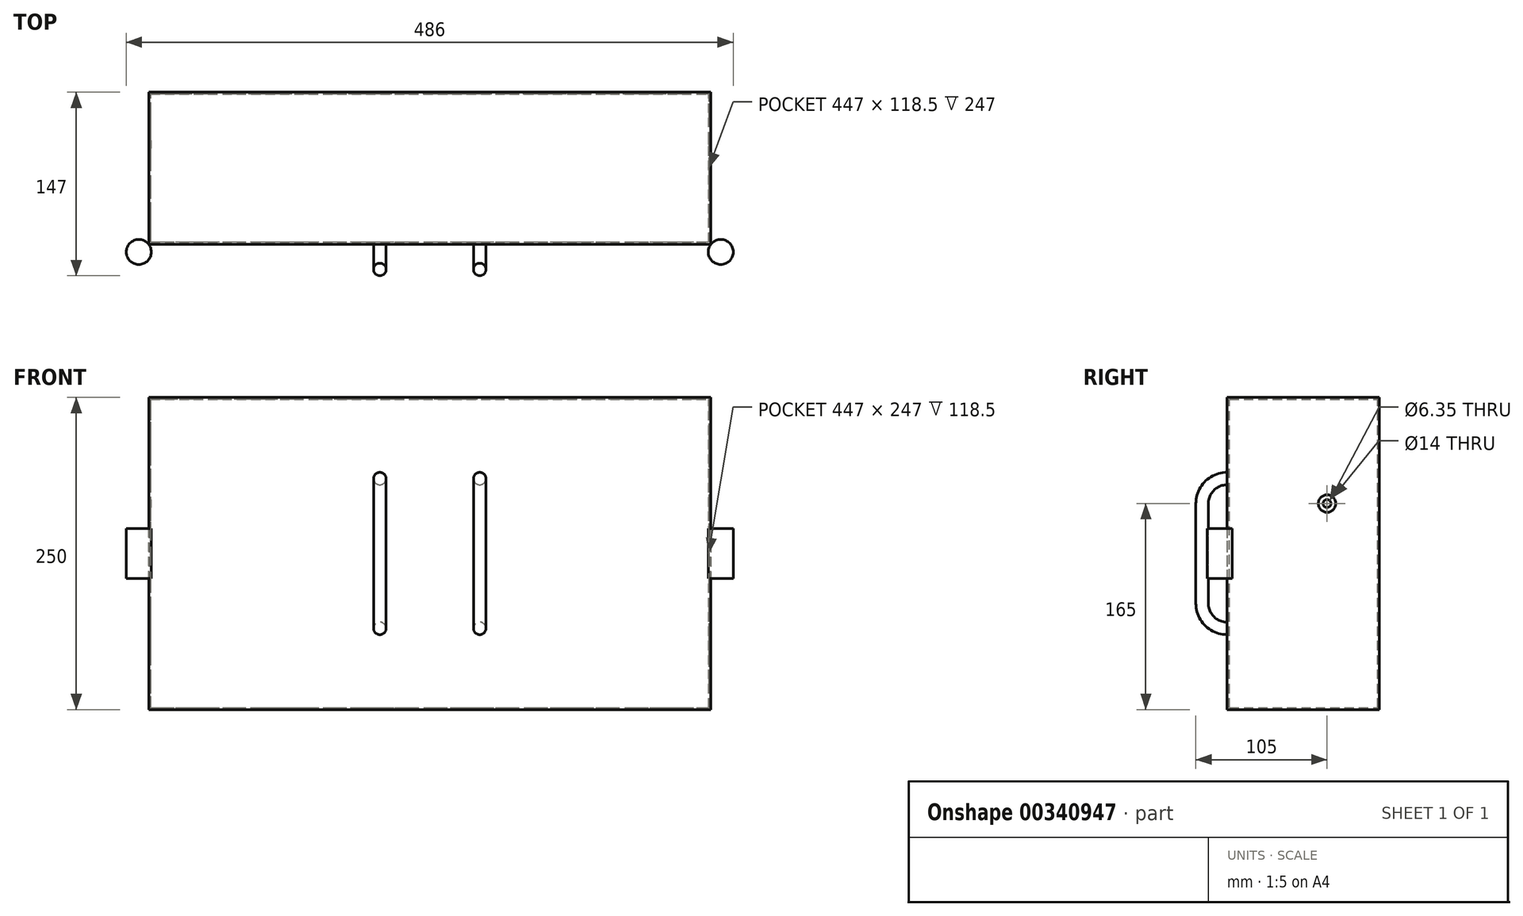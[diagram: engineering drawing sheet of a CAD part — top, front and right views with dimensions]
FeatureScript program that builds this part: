
annotation { "Feature Type Name" : "Feature", "Feature Type Description" : "" }
export const myFeature = defineFeature(function(context is Context, id is Id, definition is map)
    precondition{}
    {
        {
            var Q0;
            Q0=qCreatedBy(makeId("Front.planeOp"),FACE);
            var sketch = newSketch(context, id + "F0", { "sketchPlane" : qUnion([Q0])});
            skLineSegment(sketch, "E0.bottom", {"start": v(-225, -125) * mm, "end": v(225, -125) * mm});
            skLineSegment(sketch, "E0.top", {"start": v(-225, 125) * mm, "end": v(225, 125) * mm});
            skLineSegment(sketch, "E0.left", {"start": v(-225, -125) * mm, "end": v(-225, 125) * mm});
            skLineSegment(sketch, "E0.right", {"start": v(225, -125) * mm, "end": v(225, 125) * mm});
            skPoint(sketch, "E0.middle", {"position": v(0, 0) * mm});
            skSolve(sketch);
        }
        {
            var Q0;
            Q0 = qSketchRegion(id + "F0", true);
            extrude(context, id + "F1", {"entities" : qUnion([Q0]), "depth" : 120 * mm});
        }
        {
            var Q0;
            Q0=makeQuery(id+"F1.opExtrude","CAP_FACE",FACE,{"disambiguationData":[OSD([sQuery(id+"F0.wireOp",EDGE,"E0.bottom"),sQuery(id+"F0.wireOp",EDGE,"E0.top"),sQuery(id+"F0.wireOp",EDGE,"E0.left"),sQuery(id+"F0.wireOp",EDGE,"E0.right")])],"isStart":false});
            shell(context, id + "F2", {"entities" : qUnion([Q0]), "thickness" : 1.5 * mm});
        }
        {
            var Q0;
            Q0=makeQuery(id+"F1.opExtrude","SWEPT_FACE",FACE,{"disambiguationData":[OSD([sQuery(id+"F0.wireOp",EDGE,"E0.left")])]});
            var sketch = newSketch(context, id + "F3", { "sketchPlane" : qUnion([Q0])});
            skCircle(sketch, "E1", {"center": v(42, 40) * mm, "radius": 3.18 * mm});
            skSolve(sketch);
        }
        {
            var Q0;
            Q0 = qSketchRegion(id + "F3", true);
            extrude(context, id + "F4", {"entities" : qUnion([Q0]), "operationType" : NewBodyOperationType.REMOVE, "oppositeDirection" : true, "depth" : 555 * mm});
        }
        {
            var Q0;
            Q0=makeQuery(id+"F1.opExtrude","SWEPT_FACE",FACE,{"disambiguationData":[OSD([sQuery(id+"F0.wireOp",EDGE,"E0.right")])]});
            var sketch = newSketch(context, id + "F5", { "sketchPlane" : qUnion([Q0])});
            skCircle(sketch, "E2", {"center": v(-42, 40) * mm, "radius": 7 * mm});
            skSolve(sketch);
        }
        {
            var Q0;
            Q0 = qSketchRegion(id + "F5", true);
            extrude(context, id + "F6", {"entities" : qUnion([Q0]), "operationType" : NewBodyOperationType.REMOVE, "oppositeDirection" : true, "depth" : 5 * mm});
        }
        {
            var Q0;
            Q0=qCreatedBy(makeId("Top.planeOp"),FACE);
            var sketch = newSketch(context, id + "F7", { "sketchPlane" : qUnion([Q0])});
            skCircle(sketch, "E3", {"center": v(-233, -128) * mm, "radius": 10 * mm});
            skLineSegment(sketch, "E4.0", {"start": v(-225, -120) * mm, "end": v(-225, 0) * mm});
            skLineSegment(sketch, "E5.0", {"start": v(-225, -120) * mm, "end": v(225, -120) * mm});
            skCircle(sketch, "E6", {"center": v(233, -128) * mm, "radius": 10 * mm});
            skLineSegment(sketch, "E7", {"start": v(-225, -120) * mm, "end": v(-225, -122) * mm});
            skLineSegment(sketch, "E8", {"start": v(225, -120) * mm, "end": v(225, -122) * mm});
            skLineSegment(sketch, "E9", {"start": v(225, -122) * mm, "end": v(-225, -122) * mm});
            skSolve(sketch);
        }
        {
            var Q0;
            Q0=makeQuery(id+"F7.imprint","IMPRINT",FACE,{"disambiguationData":[TD([[makeQuery(id+"F7.imprint","IMPRINT",EDGE,{"derivedFrom":sQuery(id+"F7.wireOp",EDGE,"E5.0")}),-1.0]])]});
            var Q1;
            Q1=makeQuery(id+"F1.opExtrude","SWEPT_FACE",FACE,{"disambiguationData":[OSD([sQuery(id+"F0.wireOp",EDGE,"E0.top")])]});
            var Q2;
            Q2=makeQuery(id+"F1.opExtrude","SWEPT_FACE",FACE,{"disambiguationData":[OSD([sQuery(id+"F0.wireOp",EDGE,"E0.bottom")])]});
            extrude(context, id + "F8", {"entities" : qUnion([Q0]), "operationType" : NewBodyOperationType.ADD, "endBound" : BoundingType.UP_TO_SURFACE, "endBoundEntityFace" : qUnion([Q1]), "depth" : 25 * mm, "hasSecondDirection" : true, "secondDirectionBound" : SecondDirectionBoundingType.UP_TO_SURFACE, "secondDirectionOppositeDirection" : true, "secondDirectionBoundEntityFace" : qUnion([Q2]), "secondDirectionDepth" : 25 * mm});
        }
        {
            var Q0;
            Q0=qCreatedBy(makeId("Right.planeOp"),FACE);
            cPlane(context, id + "F9", {"entities" : qUnion([Q0]), "cplaneType" : CPlaneType.OFFSET, "offset" : 40 * mm, "width" : 150 * mm, "height" : 150 * mm});
        }
        {
            var Q0;
            Q0=qCreatedBy(id+"F9.planeOp",FACE);
            var sketch = newSketch(context, id + "F10", { "sketchPlane" : qUnion([Q0])});
            skArc(sketch, "E10.0", {"start": v(-121.76, 60) * mm, "mid": v(-136.06, 54.23) * mm, "end": v(-142, 40) * mm});
            skLineSegment(sketch, "E11.0", {"start": v(-142, 40) * mm, "end": v(-142, -40) * mm});
            skArc(sketch, "E12.0", {"start": v(-142, -40) * mm, "mid": v(-136.06, -54.23) * mm, "end": v(-121.76, -60) * mm});
            skSolve(sketch);
        }
        {
            var Q0;
            Q0=qCreatedBy(makeId("Right.planeOp"),FACE);
            cPlane(context, id + "F11", {"entities" : qUnion([Q0]), "cplaneType" : CPlaneType.OFFSET, "offset" : 40 * mm, "oppositeDirection" : true, "width" : 150 * mm, "height" : 150 * mm});
        }
        {
            var Q0;
            Q0=qCreatedBy(id+"F11.planeOp",FACE);
            var sketch = newSketch(context, id + "F12", { "sketchPlane" : qUnion([Q0])});
            skArc(sketch, "E13.0", {"start": v(-121.76, 60) * mm, "mid": v(-136.06, 54.23) * mm, "end": v(-142, 40) * mm});
            skLineSegment(sketch, "E14.0", {"start": v(-142, 40) * mm, "end": v(-142, -40) * mm});
            skPoint(sketch, "E15.0", {"position": v(-136.06, -54.23) * mm});
            skArc(sketch, "E16.0", {"start": v(-142, -40) * mm, "mid": v(-136.06, -54.23) * mm, "end": v(-121.76, -60) * mm});
            skSolve(sketch);
        }
        {
            var Q0;
            Q0=makeQuery(id+"F8.opExtrude","SWEPT_FACE",FACE,{"disambiguationData":[OSD([sQuery(id+"F7.wireOp",EDGE,"E9")])]});
            var sketch = newSketch(context, id + "F13", { "sketchPlane" : qUnion([Q0])});
            skPoint(sketch, "E17.0", {"position": v(-40, -60) * mm});
            skPoint(sketch, "E18.0", {"position": v(40, -60) * mm});
            skCircle(sketch, "E19", {"center": v(-40, -60) * mm, "radius": 5 * mm});
            skCircle(sketch, "E20", {"center": v(40, -60) * mm, "radius": 5 * mm});
            skSolve(sketch);
        }
        {
            var Q0;
            Q0=makeQuery(id+"F13.imprint","IMPRINT",FACE,{"disambiguationData":[TD([[makeQuery(id+"F13.imprint","IMPRINT",EDGE,{"derivedFrom":sQuery(id+"F13.wireOp",EDGE,"E19")}),1.0]])]});
            var Q1;
            Q1=sQuery(id+"F12.wireOp",EDGE,"E14.0");
            var Q2;
            Q2=sQuery(id+"F12.wireOp",EDGE,"E16.0");
            var Q3;
            Q3=sQuery(id+"F12.wireOp",EDGE,"E13.0");
            sweep(context, id + "F14", {"operationType" : NewBodyOperationType.ADD, "profiles" : qUnion([Q0]), "path" : qUnion([Q1, Q2, Q3])});
        }
        {
            var Q0;
            Q0=makeQuery(id+"F13.imprint","IMPRINT",FACE,{"disambiguationData":[TD([[makeQuery(id+"F13.imprint","IMPRINT",EDGE,{"derivedFrom":sQuery(id+"F13.wireOp",EDGE,"E20")}),1.0]])]});
            var Q1;
            Q1=sQuery(id+"F10.wireOp",EDGE,"E12.0");
            var Q2;
            Q2=sQuery(id+"F10.wireOp",EDGE,"E11.0");
            var Q3;
            Q3=sQuery(id+"F10.wireOp",EDGE,"E10.0");
            sweep(context, id + "F15", {"operationType" : NewBodyOperationType.ADD, "profiles" : qUnion([Q0]), "path" : qUnion([Q1, Q2, Q3])});
        }
        {
            var Q0;
            Q0=makeQuery(id+"F7.imprint","IMPRINT",FACE,{"disambiguationData":[TD([[makeQuery(id+"F7.imprint","IMPRINT",EDGE,{"derivedFrom":sQuery(id+"F7.wireOp",EDGE,"E3")}),1.0]])]});
            var Q1;
            Q1=makeQuery(id+"F7.imprint","IMPRINT",FACE,{"disambiguationData":[TD([[makeQuery(id+"F7.imprint","IMPRINT",EDGE,{"derivedFrom":sQuery(id+"F7.wireOp",EDGE,"E6")}),1.0]])]});
            extrude(context, id + "F16", {"entities" : qUnion([Q0, Q1]), "depth" : 20 * mm, "hasSecondDirection" : true, "secondDirectionOppositeDirection" : true, "secondDirectionDepth" : 20 * mm});
        }
    });
